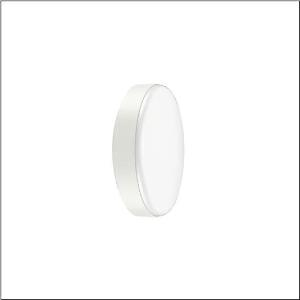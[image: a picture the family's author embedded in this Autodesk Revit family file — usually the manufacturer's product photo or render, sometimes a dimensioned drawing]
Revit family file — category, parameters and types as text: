
# Revit family: rondel_31_51wc10da42a
name_source: partatom
category: Lighting Fixtures
units: mm (PartAtom-declared; Revit-internal decimal feet)

## family parameters
Cut with Voids When Loaded = No
Host = Face
Light Source = No
Part Type = Normal
Room Calculation Point = No
Round Connector Dimension = Use Diameter
Shared = No

## types (1)
- Rondel 31 (1 x LED, 2550 lm, 19 W, 4000K)
    Apparent Load = 19 VA
    CIE Flux Codes = 44 75 94 94 100
    Color Rendering = 80
    Color Temperature = 4000K
    Default Elevation = 1800 mm
    Description = Rondel 31, wall and ceiling luminaire, primary optical cover: cover, of PC, opal, light emission: direct distribution, primary light characteristic: symmetric, installation type: surface-mounted, LED, rated luminous flux: 2.550lm, luminous efficacy: 134lm/W, light colour: 840, colour temperature: 4000K, with terminal, 5-pole, max. 2.5mm², mains connection: 220..240V, AC, 50/60Hz, rated input power: 19W, luminaire housing, of PC, traffic white (RAL 9016), diameter: 350mm, protection rating (complete): IP65, insulation class (complete): insulation class II (safety insulation), certification: CE, impact resistance: IK10, permissible operating ambient temperature: -20..+40°C, permissible storage temperature: -20..+60°C, packaging unit: 1 piece
    Height = 97 mm
    Lamp = 1 x LED
    Lamp Light Flux = 2550 lm
    Lamp Power = 19 W
    Lamp count = 1
    Length = 350 mm
    Luminous efficacy = 134 lm/W
    Manufacturer = Siteco
    ModVariant = No
    Model = 51WC10DA42A
    Mounting Place = Ceiling
    Mounting Type = Surface mounted
    Number of Poles = 1
    OnlyDefault = Yes
    Power Factor = 1
    Product Name = Rondel 31
    Product group = wall and ceiling luminaire
    ProductGroupID = 301
    Protection Class = Protection class II
    Protection Degree = IP 65
    RLX_Detail_Level = 1
    RLX_Emergency_Light_Flux = 0 lm
    RLX_Emergency_Type = 0
    RLX_Emergency_Type_DB = No
    RlxData = <blob elided: 29757 chars, md5=a36b48b7>
    Socket = socket
    Standby Power = 0 W
    System Light Flux = 2550 lm
    System Power = 19 W
    Type Comments = Product without accessories
    Type Image = l_1007027.jpg
    URL = http://relux.com
    VarID = ---
    Voltage = 0 V
    Weight = 0.00 kg
    Width = 0 mm  [stored 0 ft]

note: [stored X ft] marks values corroborated as IEEE doubles in the binary element streams (Revit-internal decimal feet)

## geometry (parser evidence)
native form markers: Blend x4, Sweep x13
no freeform markers — native parametric forms only
